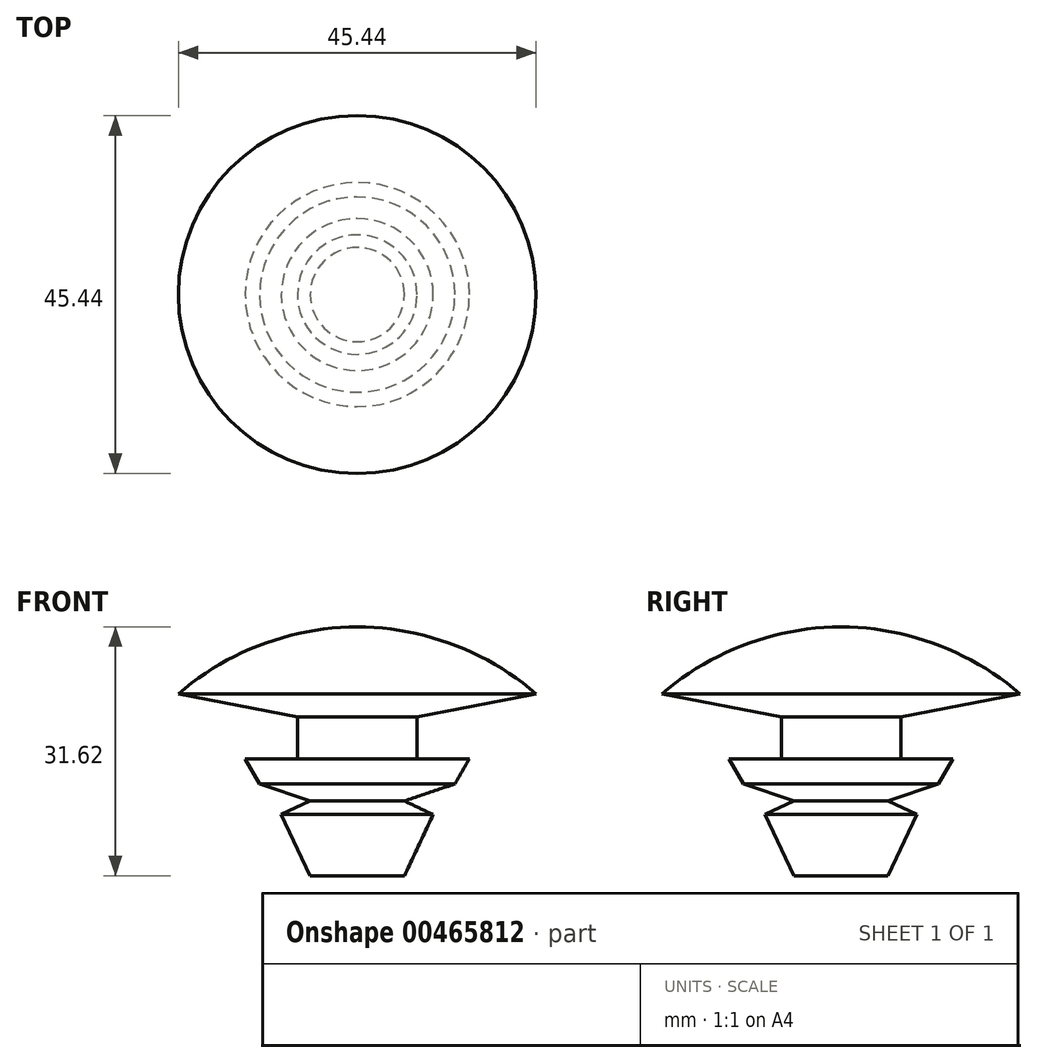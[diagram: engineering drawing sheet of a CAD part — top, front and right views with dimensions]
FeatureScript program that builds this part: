
annotation { "Feature Type Name" : "Feature", "Feature Type Description" : "" }
export const myFeature = defineFeature(function(context is Context, id is Id, definition is map)
    precondition{}
    {
        {
            var Q0;
            Q0=qCreatedBy(makeId("Front.planeOp"),FACE);
            var sketch = newSketch(context, id + "F0", { "sketchPlane" : qUnion([Q0])});
            skLineSegment(sketch, "E0", {"start": v(0, 0) * mm, "end": v(5.98, 0) * mm});
            skLineSegment(sketch, "E1", {"start": v(5.98, 0) * mm, "end": v(9.65, 7.77) * mm});
            skLineSegment(sketch, "E2", {"start": v(9.65, 7.77) * mm, "end": v(5.98, 9.5) * mm});
            skLineSegment(sketch, "E3", {"start": v(5.98, 9.5) * mm, "end": v(12.4, 11.67) * mm});
            skLineSegment(sketch, "E4", {"start": v(12.4, 11.67) * mm, "end": v(14.24, 14.88) * mm});
            skLineSegment(sketch, "E5", {"start": v(14.24, 14.88) * mm, "end": v(7.59, 14.88) * mm});
            skLineSegment(sketch, "E6", {"start": v(7.59, 14.88) * mm, "end": v(7.59, 20.15) * mm});
            skLineSegment(sketch, "E7", {"start": v(7.59, 20.15) * mm, "end": v(22.72, 23.14) * mm});
            skArc(sketch, "E8", {"start": v(22.72, 23.14) * mm, "mid": v(12.12, 29.4) * mm, "end": v(0, 31.62) * mm});
            skLineSegment(sketch, "E9", {"start": v(0, 31.62) * mm, "end": v(0, 0) * mm});
            skSolve(sketch);
        }
        {
            var Q0;
            Q0=makeQuery(id+"F0.imprint","IMPRINT",FACE,{"disambiguationData":[TD([[makeQuery(id+"F0.imprint","IMPRINT",EDGE,{"derivedFrom":sQuery(id+"F0.wireOp",EDGE,"E0")}),1.0]])]});
            var Q1;
            Q1=sQuery(id+"F0.wireOp",EDGE,"E9");
            revolve(context, id + "F1", {"entities" : qUnion([Q0]), "axis" : qUnion([Q1]), "revolveType" : RevolveType.FULL});
        }
    });
